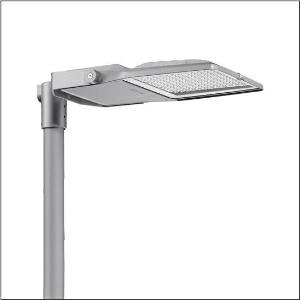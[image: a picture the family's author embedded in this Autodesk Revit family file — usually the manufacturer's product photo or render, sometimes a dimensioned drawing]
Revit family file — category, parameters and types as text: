
# Revit family: floodlight_fl_21_iq_midi___pl64_5xa7781f2e3a_9caf
name_source: partatom
category: Lighting Fixtures
units: mm (PartAtom-declared; Revit-internal decimal feet)

## family parameters
Cut with Voids When Loaded = No
Host = Face
Light Source = No
Part Type = Normal
Room Calculation Point = No
Round Connector Dimension = Use Diameter
Shared = No

## types (1)
- --- (1 x LED, 34530 lm, 270.2 W, 3000K)
    Apparent Load = 270 VA
    CIE Flux Codes = 28 80 98 100 100
    Color Rendering = 70
    Color Temperature = 3000K
    Default Elevation = 1800 mm
    Description = Floodlight FL 21 iQ midi, floodlight, primary light control with lens, of PMMA, primary optical cover: protective disc, of toughened safety glass, transparent, light distribution: PL64, light emission: direct distribution, installation type: surface-mounted, LED, High Power LED, rated luminous flux: 34.530lm, luminous efficacy: 128lm/W, light colour: 730, colour temperature: 3000K, control gear: ECG iQ, control: optimised constant luminous flux control (CLO 2.0), Desk-Remote (wireless, voltage-free reading and setting of iQ features in the workshop via application-optimized NFC function/RFID function), Light-Fading, Smart-Wire, Night-Set, Lumen-Switch, Temp-Guard, Auto-Match, with terminal, 6-pole, mains connection: 220..240V, AC, 50/60Hz, start of lifetime: 270W, end of service life: 287W, reduction: 117W, luminaire housing, of diecast aluminium, powder-coated, Siteco® metallic grey (DB 702S), corrosivity category C5 mid according to DIN EN ISO 12944, sealing non-destructively replaceable, please order mast flange separately, mast bracket, of steel, galvanised, powder-coated, Siteco® metallic grey (DB 702S), protection rating (complete): IP66, insulation class (complete): insulation class II (safety insulation), certification: CE, protection symbol: D, impact resistance: IK08, permissible operating ambient temperature: -40..+40°C, permissible operating ambient temperature for outdoor applications: -40..+50°C, standard: DIN EN 12944, LABS conformity tested according to VDMA 24364:2018-05, packaging unit: 1 piece

Light Distribution: PL64
    Height = 76 mm
    Lamp = 1 x LED
    Lamp Light Flux = 34530 lm
    Lamp Power = 270.2 W
    Lamp count = 1
    Length = 657 mm
    Luminous efficacy = 128 lm/W
    Manufacturer = Siteco
    ModVariant = No
    Model = 5XA7781F2E3A
    Number of Poles = 1
    OnlyDefault = Yes
    Power Factor = 1
    Product Name = Floodlight FL 21 iQ midi | PL64
    Product group = floodlight | pylon annexe
    ProductGroupID = 6200
    Protection Class = Protection class II
    Protection Degree = IP 66
    RLX_Detail_Level = 1
    RLX_Emergency_Light_Flux = 0 lm
    RLX_Emergency_Type = 0
    RLX_Emergency_Type_DB = No
    RlxData = <blob elided: 153581 chars, md5=4237a0ff>
    Socket = socket
    Standby Power = 0 W
    System Light Flux = 34530 lm
    System Power = 270 W
    Type Comments = factory setting: luminous flux: 100 % | dim-lin: 254 | 620 mA
    Type Image = l_1007123.jpg
    URL = http://relux.com
    VarID = @adj_036995
    Voltage = 0 V
    Weight = 0.00 kg
    Width = 442 mm

## geometry (parser evidence)
native form markers: Blend x4, Sweep x13
no freeform markers — native parametric forms only
